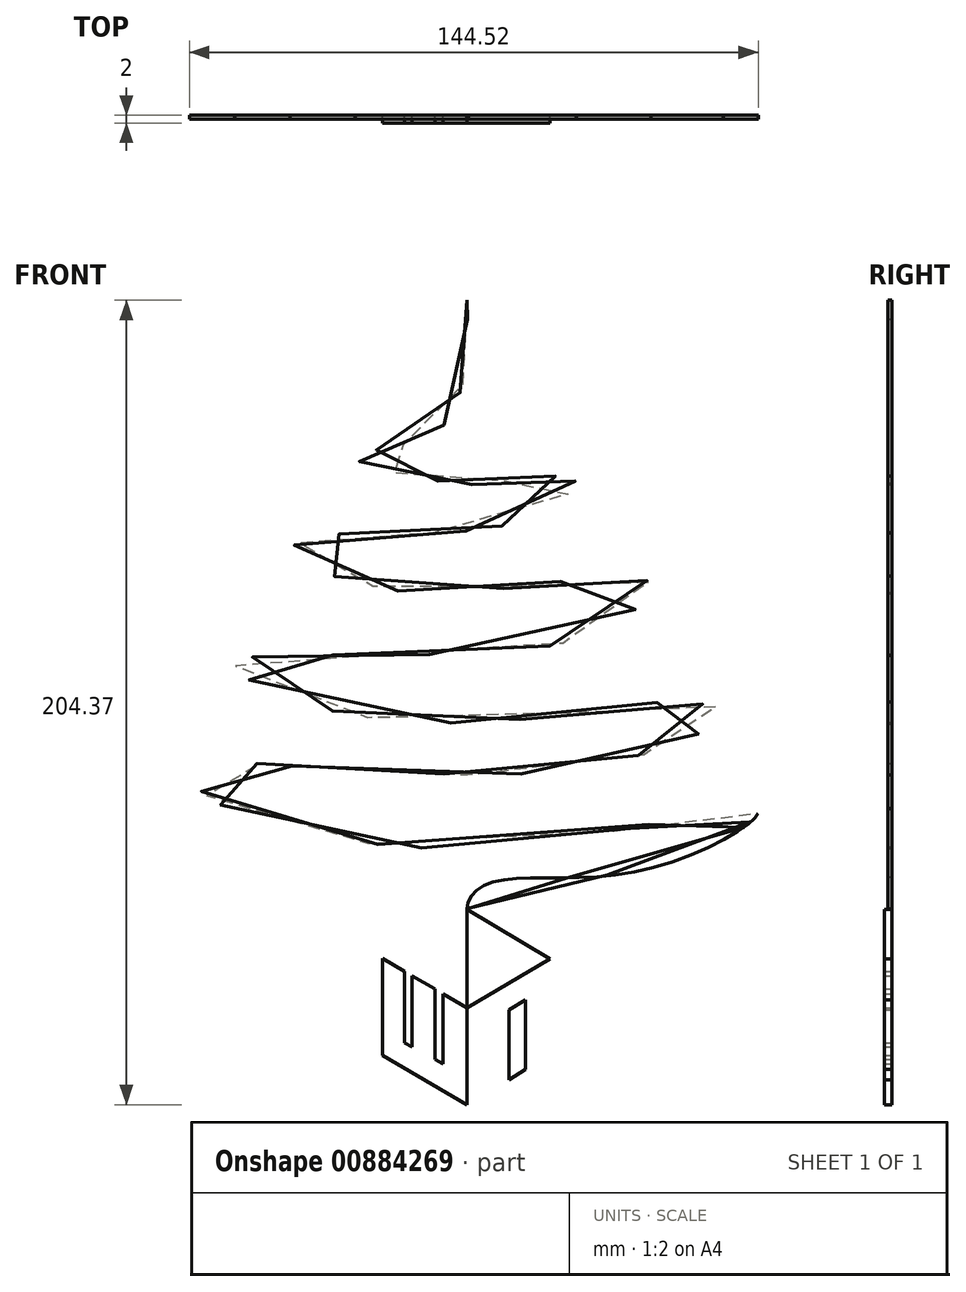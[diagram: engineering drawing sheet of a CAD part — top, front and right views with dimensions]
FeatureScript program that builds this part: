
annotation { "Feature Type Name" : "Feature", "Feature Type Description" : "" }
export const myFeature = defineFeature(function(context is Context, id is Id, definition is map)
    precondition{}
    {
        {
            var Q0;
            Q0=qCreatedBy(makeId("Front.planeOp"),FACE);
            var sketch = newSketch(context, id + "F0", { "sketchPlane" : qUnion([Q0])});
            skFitSpline(sketch, "E0", {"points": [v(0, 110.63) * mm, v(0, 94.95) * mm, v(-2.18, 85.8) * mm, v(-9.83, 75.87) * mm, v(-28.22, 70.95) * mm, v(-7.95, 64.75) * mm, v(9.72, 64.91) * mm, v(27.67, 64.86) * mm, v(10.6, 53.78) * mm, v(-29.88, 51.5) * mm, v(-44.77, 46.54) * mm, v(-17.88, 37.03) * mm, v(22.73, 39.23) * mm, v(46.52, 38.6) * mm, v(34.25, 26.69) * mm, v(-30.3, 20.48) * mm, v(-58.84, 17.59) * mm, v(-19.95, 3.93) * mm, v(47.76, 8.4) * mm, v(65.11, 5.77) * mm, v(43.76, -5.17) * mm, v(-19.54, -9.3) * mm, v(-70, -9.3) * mm, v(-62.15, -17.58) * mm, v(12.18, -27.59) * mm, v(73.96, -19.23) * mm, v(45, -34.13) * mm, v(5.7, -37.44) * mm, v(0, -43.97) * mm], "startDerivative": vector(47.67, -524.44) * mm, "endDerivative": vector(0, -398.03) * mm});
            skFitSpline(sketch, "E1.0", {"points": [v(-0.2, 110.6) * mm, v(-0.14, 109.93) * mm, v(-0.03, 108.48) * mm, v(0.1, 106.15) * mm, v(0.15, 103.7) * mm, v(0.16, 101.24) * mm, v(0.1, 99.22) * mm, v(0.03, 97.66) * mm, v(-0.05, 96.53) * mm, v(-0.13, 95.62) * mm, v(-0.2, 94.92) * mm, v(-0.28, 94.25) * mm, v(-0.4, 93.44) * mm, v(-0.56, 92.5) * mm, v(-0.73, 91.62) * mm, v(-0.99, 90.47) * mm, v(-1.28, 89.37) * mm, v(-1.6, 88.28) * mm, v(-1.85, 87.45) * mm, v(-2.08, 86.76) * mm, v(-2.26, 86.2) * mm, v(-2.45, 85.62) * mm, v(-2.7, 84.89) * mm, v(-3.01, 84) * mm, v(-3.36, 83.1) * mm, v(-3.9, 81.9) * mm, v(-4.7, 80.43) * mm, v(-6, 78.77) * mm, v(-7.42, 77.5) * mm, v(-8.81, 76.6) * mm, v(-10, 76) * mm, v(-11.34, 75.45) * mm, v(-13.3, 74.8) * mm, v(-15.42, 74.26) * mm, v(-17.6, 73.8) * mm, v(-19.22, 73.5) * mm, v(-20.8, 73.22) * mm, v(-22.33, 72.95) * mm, v(-23.74, 72.7) * mm, v(-25.03, 72.46) * mm, v(-25.96, 72.25) * mm, v(-26.62, 72.08) * mm, v(-27.06, 71.95) * mm, v(-27.44, 71.81) * mm, v(-27.77, 71.67) * mm, v(-28.04, 71.51) * mm, v(-28.22, 71.36) * mm, v(-28.33, 71.23) * mm, v(-28.39, 71.11) * mm, v(-28.43, 70.99) * mm, v(-28.43, 70.85) * mm, v(-28.4, 70.73) * mm, v(-28.36, 70.6) * mm, v(-28.3, 70.49) * mm, v(-28.19, 70.34) * mm, v(-28, 70.16) * mm, v(-27.73, 69.95) * mm, v(-27.4, 69.74) * mm, v(-27, 69.53) * mm, v(-26.56, 69.31) * mm, v(-25.9, 69.02) * mm, v(-24.94, 68.65) * mm, v(-23.63, 68.2) * mm, v(-22.17, 67.73) * mm, v(-20.6, 67.28) * mm, v(-18.38, 66.69) * mm, v(-16.04, 66.12) * mm, v(-13.68, 65.6) * mm, v(-11.93, 65.25) * mm, v(-10.5, 64.98) * mm, v(-9.4, 64.78) * mm, v(-8.6, 64.65) * mm, v(-7.81, 64.52) * mm, v(-7.06, 64.41) * mm, v(-6.33, 64.3) * mm, v(-5.4, 64.19) * mm, v(-4.28, 64.07) * mm, v(-3, 63.96) * mm, v(-1.8, 63.9) * mm, v(-0.24, 63.85) * mm, v(1.26, 63.88) * mm, v(2.75, 63.96) * mm, v(3.88, 64.04) * mm, v(5.03, 64.15) * mm, v(6.22, 64.28) * mm, v(7.26, 64.4) * mm, v(8.13, 64.51) * mm, v(8.8, 64.6) * mm, v(9.49, 64.68) * mm, v(10.2, 64.77) * mm, v(10.93, 64.86) * mm, v(11.93, 64.98) * mm, v(13.22, 65.14) * mm, v(14.8, 65.31) * mm, v(16.4, 65.48) * mm, v(18.51, 65.67) * mm, v(20.55, 65.8) * mm, v(22.4, 65.85) * mm, v(23.7, 65.83) * mm, v(24.85, 65.76) * mm, v(25.83, 65.62) * mm, v(26.5, 65.44) * mm, v(26.91, 65.27) * mm, v(27.17, 65.12) * mm, v(27.36, 64.96) * mm, v(27.46, 64.83) * mm, v(27.52, 64.71) * mm, v(27.56, 64.59) * mm, v(27.59, 64.42) * mm, v(27.57, 64.2) * mm, v(27.5, 63.93) * mm, v(27.36, 63.64) * mm, v(27.11, 63.22) * mm, v(26.67, 62.65) * mm, v(25.93, 61.91) * mm, v(25.02, 61.13) * mm, v(23.94, 60.31) * mm, v(22.71, 59.48) * mm, v(20.9, 58.36) * mm, v(18.85, 57.26) * mm, v(16.64, 56.22) * mm, v(14.9, 55.49) * mm, v(13.13, 54.8) * mm, v(11.6, 54.3) * mm, v(10.39, 53.92) * mm, v(9.16, 53.58) * mm, v(7.62, 53.2) * mm, v(5.75, 52.82) * mm, v(3.26, 52.4) * mm, v(0.1, 52.03) * mm, v(-3.69, 51.78) * mm, v(-7.5, 51.7) * mm, v(-11.3, 51.7) * mm, v(-15.1, 51.78) * mm, v(-18.85, 51.87) * mm, v(-22.56, 51.93) * mm, v(-26.22, 51.9) * mm, v(-29.8, 51.75) * mm, v(-33.3, 51.41) * mm, v(-36.59, 50.92) * mm, v(-39.03, 50.38) * mm, v(-40.75, 49.88) * mm, v(-41.9, 49.47) * mm, v(-42.9, 49.03) * mm, v(-43.72, 48.55) * mm, v(-44.25, 48.13) * mm, v(-44.58, 47.76) * mm, v(-44.78, 47.48) * mm, v(-44.91, 47.17) * mm, v(-44.98, 46.86) * mm, v(-44.98, 46.54) * mm, v(-44.91, 46.21) * mm, v(-44.78, 45.9) * mm, v(-44.52, 45.48) * mm, v(-44.05, 44.96) * mm, v(-43.29, 44.34) * mm, v(-42.33, 43.72) * mm, v(-41.2, 43.1) * mm, v(-39.9, 42.48) * mm, v(-38.46, 41.87) * mm, v(-36.36, 41.07) * mm, v(-33.44, 40.11) * mm, v(-29.6, 39.05) * mm, v(-26.2, 38.26) * mm, v(-23.45, 37.7) * mm, v(-21.37, 37.34) * mm, v(-19.64, 37.07) * mm, v(-18.27, 36.88) * mm, v(-16.9, 36.7) * mm, v(-15.23, 36.52) * mm, v(-13.25, 36.35) * mm, v(-11.29, 36.23) * mm, v(-8.71, 36.12) * mm, v(-5.55, 36.1) * mm, v(-1.82, 36.2) * mm, v(1.86, 36.44) * mm, v(5.5, 36.78) * mm, v(9.14, 37.2) * mm, v(12.78, 37.67) * mm, v(15.84, 38.09) * mm, v(18.32, 38.43) * mm, v(20.19, 38.69) * mm, v(21.76, 38.9) * mm, v(23.03, 39.07) * mm, v(24.3, 39.23) * mm, v(25.9, 39.43) * mm, v(27.83, 39.66) * mm, v(29.73, 39.86) * mm, v(32.23, 40.1) * mm, v(35.24, 40.33) * mm, v(38.55, 40.44) * mm, v(40.97, 40.36) * mm, v(42.65, 40.18) * mm, v(43.75, 39.98) * mm, v(44.7, 39.7) * mm, v(45.33, 39.42) * mm, v(45.74, 39.16) * mm, v(46, 38.95) * mm, v(46.21, 38.72) * mm, v(46.37, 38.48) * mm, v(46.48, 38.22) * mm, v(46.56, 37.84) * mm, v(46.56, 37.3) * mm, v(46.37, 36.59) * mm, v(46, 35.8) * mm, v(45.45, 34.94) * mm, v(44.5, 33.75) * mm, v(42.9, 32.2) * mm, v(40.45, 30.3) * mm, v(38.02, 28.79) * mm, v(35.87, 27.65) * mm, v(34.17, 26.85) * mm, v(32.39, 26.12) * mm, v(29.9, 25.2) * mm, v(26.63, 24.21) * mm, v(22.43, 23.23) * mm, v(16.53, 22.17) * mm, v(8.66, 21.27) * mm, v(0.35, 20.8) * mm, v(-6.45, 20.62) * mm, v(-11.58, 20.56) * mm, v(-16.72, 20.56) * mm, v(-20.99, 20.59) * mm, v(-24.38, 20.62) * mm, v(-26.9, 20.65) * mm, v(-29.4, 20.67) * mm, v(-31.87, 20.7) * mm, v(-34.31, 20.71) * mm, v(-37.5, 20.73) * mm, v(-41.35, 20.72) * mm, v(-45.63, 20.64) * mm, v(-48.85, 20.5) * mm, v(-51.16, 20.34) * mm, v(-52.76, 20.2) * mm, v(-54.2, 20) * mm, v(-55.47, 19.79) * mm, v(-56.57, 19.52) * mm, v(-57.49, 19.22) * mm, v(-58.1, 18.92) * mm, v(-58.47, 18.65) * mm, v(-58.7, 18.43) * mm, v(-58.89, 18.19) * mm, v(-59, 17.92) * mm, v(-59.04, 17.67) * mm, v(-59.03, 17.48) * mm, v(-59, 17.28) * mm, v(-58.92, 17.03) * mm, v(-58.76, 16.72) * mm, v(-58.55, 16.42) * mm, v(-58.2, 16) * mm, v(-57.61, 15.47) * mm, v(-56.71, 14.8) * mm, v(-55.62, 14.1) * mm, v(-54.35, 13.39) * mm, v(-52.9, 12.66) * mm, v(-50.77, 11.67) * mm, v(-47.73, 10.42) * mm, v(-43.57, 8.95) * mm, v(-39, 7.54) * mm, v(-34.1, 6.25) * mm, v(-29.81, 5.3) * mm, v(-26.32, 4.65) * mm, v(-23.67, 4.22) * mm, v(-21.45, 3.91) * mm, v(-19.68, 3.7) * mm, v(-17.9, 3.5) * mm, v(-15.69, 3.31) * mm, v(-13.03, 3.14) * mm, v(-10.39, 3.03) * mm, v(-6.87, 2.96) * mm, v(-2.5, 3) * mm, v(2.7, 3.23) * mm, v(7.82, 3.6) * mm, v(14.55, 4.25) * mm, v(21.1, 5.06) * mm, v(27.44, 5.91) * mm, v(32.05, 6.54) * mm, v(36.53, 7.12) * mm, v(40.14, 7.55) * mm, v(42.94, 7.83) * mm, v(45, 8.02) * mm, v(46.67, 8.14) * mm, v(48, 8.22) * mm, v(49.3, 8.29) * mm, v(50.9, 8.35) * mm, v(53.36, 8.39) * mm, v(56.24, 8.34) * mm, v(58.77, 8.15) * mm, v(60.53, 7.9) * mm, v(61.7, 7.68) * mm, v(62.72, 7.42) * mm, v(63.56, 7.11) * mm, v(64.1, 6.83) * mm, v(64.44, 6.58) * mm, v(64.63, 6.4) * mm, v(64.78, 6.2) * mm, v(64.87, 6.01) * mm, v(64.92, 5.81) * mm, v(64.92, 5.6) * mm, v(64.87, 5.38) * mm, v(64.74, 5.05) * mm, v(64.45, 4.59) * mm, v(63.9, 3.99) * mm, v(63.15, 3.35) * mm, v(62.23, 2.69) * mm, v(61.15, 2) * mm, v(59.92, 1.3) * mm, v(58.1, 0.35) * mm, v(55.52, -0.85) * mm, v(52.02, -2.26) * mm, v(48.87, -3.38) * mm, v(46.26, -4.22) * mm, v(44.6, -4.72) * mm, v(43.26, -5.1) * mm, v(41.91, -5.47) * mm, v(40.21, -5.9) * mm, v(38.16, -6.4) * mm, v(35.4, -7) * mm, v(31.89, -7.65) * mm, v(27.6, -8.31) * mm, v(23.2, -8.84) * mm, v(18.71, -9.25) * mm, v(14.12, -9.54) * mm, v(9.42, -9.73) * mm, v(4.61, -9.82) * mm, v(-0.31, -9.81) * mm, v(-5.36, -9.72) * mm, v(-9.68, -9.58) * mm, v(-13.2, -9.43) * mm, v(-15.87, -9.3) * mm, v(-18.12, -9.19) * mm, v(-19.94, -9.08) * mm, v(-21.78, -8.97) * mm, v(-24.08, -8.83) * mm, v(-26.87, -8.65) * mm, v(-29.66, -8.46) * mm, v(-33.38, -8.21) * mm, v(-37.99, -7.9) * mm, v(-43.36, -7.56) * mm, v(-48.5, -7.28) * mm, v(-53.3, -7.08) * mm, v(-57.7, -7) * mm, v(-60.94, -7.06) * mm, v(-63.25, -7.2) * mm, v(-64.82, -7.33) * mm, v(-66.22, -7.53) * mm, v(-67.44, -7.78) * mm, v(-68.48, -8.08) * mm, v(-69.18, -8.4) * mm, v(-69.65, -8.68) * mm, v(-69.94, -8.92) * mm, v(-70.18, -9.18) * mm, v(-70.36, -9.47) * mm, v(-70.48, -9.78) * mm, v(-70.53, -10.1) * mm, v(-70.52, -10.44) * mm, v(-70.44, -10.9) * mm, v(-70.2, -11.49) * mm, v(-69.74, -12.22) * mm, v(-69.1, -12.98) * mm, v(-68.29, -13.76) * mm, v(-67.33, -14.56) * mm, v(-66.23, -15.36) * mm, v(-65, -16.17) * mm, v(-63.67, -16.98) * mm, v(-62.22, -17.78) * mm, v(-60.68, -18.56) * mm, v(-59.05, -19.31) * mm, v(-56.76, -20.3) * mm, v(-53.68, -21.47) * mm, v(-49.65, -22.79) * mm, v(-45.32, -24) * mm, v(-40.7, -25.08) * mm, v(-35.8, -26.04) * mm, v(-30.65, -26.87) * mm, v(-25.27, -27.54) * mm, v(-19.68, -28.06) * mm, v(-13.89, -28.41) * mm, v(-7.92, -28.59) * mm, v(-1.8, -28.57) * mm, v(3.42, -28.4) * mm, v(7.66, -28.15) * mm, v(10.33, -27.95) * mm, v(12.48, -27.76) * mm, v(14.64, -27.56) * mm, v(17.35, -27.27) * mm, v(20.6, -26.88) * mm, v(24.95, -26.3) * mm, v(30.34, -25.5) * mm, v(36.67, -24.45) * mm, v(42.78, -23.36) * mm, v(48.6, -22.28) * mm, v(54.02, -21.26) * mm, v(58.97, -20.34) * mm, v(62.64, -19.7) * mm, v(65.26, -19.29) * mm, v(67.05, -19.03) * mm, v(68.66, -18.84) * mm, v(70.07, -18.72) * mm, v(71.29, -18.67) * mm, v(72.12, -18.7) * mm, v(72.66, -18.75) * mm, v(73.01, -18.82) * mm, v(73.3, -18.9) * mm, v(73.52, -19) * mm, v(73.64, -19.1) * mm, v(73.71, -19.18) * mm, v(73.75, -19.24) * mm, v(73.77, -19.3) * mm, v(73.8, -19.39) * mm, v(73.8, -19.52) * mm, v(73.75, -19.72) * mm, v(73.64, -19.95) * mm, v(73.47, -20.22) * mm, v(73.18, -20.61) * mm, v(72.66, -21.16) * mm, v(71.84, -21.9) * mm, v(70.82, -22.68) * mm, v(69.62, -23.52) * mm, v(68.26, -24.4) * mm, v(66.25, -25.6) * mm, v(63.39, -27.15) * mm, v(59.52, -29) * mm, v(56.03, -30.45) * mm, v(53.13, -31.53) * mm, v(50.91, -32.28) * mm, v(48.67, -32.98) * mm, v(46.79, -33.5) * mm, v(45.28, -33.86) * mm, v(43.78, -34.2) * mm, v(41.91, -34.57) * mm, v(39.69, -34.93) * mm, v(37.47, -35.22) * mm, v(35.29, -35.45) * mm, v(32.4, -35.68) * mm, v(28.88, -35.85) * mm, v(24.81, -35.92) * mm, v(20.93, -35.92) * mm, v(17.28, -35.93) * mm, v(13.88, -36) * mm, v(10.78, -36.18) * mm, v(8.46, -36.5) * mm, v(6.78, -36.88) * mm, v(5.6, -37.24) * mm, v(4.54, -37.68) * mm, v(3.25, -38.36) * mm, v(1.9, -39.38) * mm, v(0.7, -40.8) * mm, v(-0.03, -42.35) * mm, v(-0.2, -43.43) * mm, v(-0.2, -43.97) * mm]});
            skLineSegment(sketch, "E2", {"start": v(0.13, 104.7) * mm, "end": v(0, 110.63) * mm});
            skLineSegment(sketch, "E3", {"start": v(-0.2, -43.97) * mm, "end": v(0, -43.97) * mm});
            skSolve(sketch);
        }
        {
            var Q0;
            Q0=qCreatedBy(makeId("Front.planeOp"),FACE);
            var sketch = newSketch(context, id + "F1", { "sketchPlane" : qUnion([Q0])});
            skLineSegment(sketch, "E4", {"start": v(0, -44.17) * mm, "end": v(0, -69.13) * mm});
            skLineSegment(sketch, "E5", {"start": v(0, -69.13) * mm, "end": v(21.12, -56.73) * mm});
            skLineSegment(sketch, "E6", {"start": v(21.12, -56.73) * mm, "end": v(0, -44.17) * mm});
            skLineSegment(sketch, "E7", {"start": v(10.69, -69.65) * mm, "end": v(14.86, -67.13) * mm});
            skLineSegment(sketch, "E8", {"start": v(14.86, -67.13) * mm, "end": v(14.86, -84.79) * mm});
            skLineSegment(sketch, "E9", {"start": v(14.86, -84.79) * mm, "end": v(10.69, -87.4) * mm});
            skLineSegment(sketch, "E10", {"start": v(10.69, -87.4) * mm, "end": v(10.69, -69.65) * mm});
            skLineSegment(sketch, "E11", {"start": v(-21.5, -56.6) * mm, "end": v(-21.5, -81.22) * mm});
            skLineSegment(sketch, "E12", {"start": v(-21.5, -81.22) * mm, "end": v(0, -93.74) * mm});
            skLineSegment(sketch, "E13", {"start": v(0, -93.74) * mm, "end": v(0, -69.13) * mm});
            skLineSegment(sketch, "E14", {"start": v(0, -69.13) * mm, "end": v(-21.5, -56.6) * mm, "construction": true});
            skLineSegment(sketch, "E15", {"start": v(-21.5, -56.6) * mm, "end": v(-15.91, -59.86) * mm});
            skLineSegment(sketch, "E16", {"start": v(-15.91, -59.86) * mm, "end": v(-15.91, -77.98) * mm});
            skLineSegment(sketch, "E17", {"start": v(-15.91, -77.98) * mm, "end": v(-13.98, -79.1) * mm});
            skLineSegment(sketch, "E18", {"start": v(-13.98, -79.1) * mm, "end": v(-13.98, -60.99) * mm});
            skLineSegment(sketch, "E19", {"start": v(-13.98, -60.99) * mm, "end": v(-8.14, -64.39) * mm});
            skLineSegment(sketch, "E20", {"start": v(-8.14, -64.39) * mm, "end": v(-8.14, -82.22) * mm});
            skLineSegment(sketch, "E21", {"start": v(-8.14, -82.22) * mm, "end": v(-6.1, -83.41) * mm});
            skLineSegment(sketch, "E22", {"start": v(-6.1, -83.41) * mm, "end": v(-6.1, -65.58) * mm});
            skLineSegment(sketch, "E23", {"start": v(-6.1, -65.58) * mm, "end": v(0, -69.13) * mm});
            skSolve(sketch);
        }
        {
            var Q0;
            Q0 = qSketchRegion(id + "F0", true);
            extrude(context, id + "F2", {"entities" : qUnion([Q0]), "depth" : 1 * mm, "offsetDistance" : 25 * mm});
        }
        {
            var Q0;
            Q0 = qSketchRegion(id + "F1", true);
            extrude(context, id + "F3", {"entities" : qUnion([Q0]), "depth" : 2 * mm, "offsetDistance" : 25 * mm});
        }
    });
